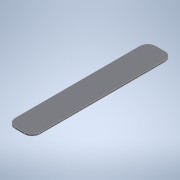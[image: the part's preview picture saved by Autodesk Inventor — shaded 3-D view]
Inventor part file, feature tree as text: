
AUTODESK INVENTOR PART (.ipt)
format: ipt  version: 2022.1 (Build 261234000, 234)  size: 107,008 bytes
history: native  units: mm
features: other x1, extrude x1, sketch x1
ambient origin geometry x8: Origin, YZ Plane, XZ Plane, XY Plane, X Axis, Y Axis, Z Axis, Center Point
bodies: Body1 (feature_tree)
feature tree (3):
  other  "Sólido1"
  extrude  "Extrusión1"  Depth=160.0mm
  sketch  "Boceto1"  dims[d0=900.0mm d1=160.0mm d2=50.0mm d3=50.0mm d4=50.0mm d5=50.0mm d6=10.0mm d7=0.0mm]
